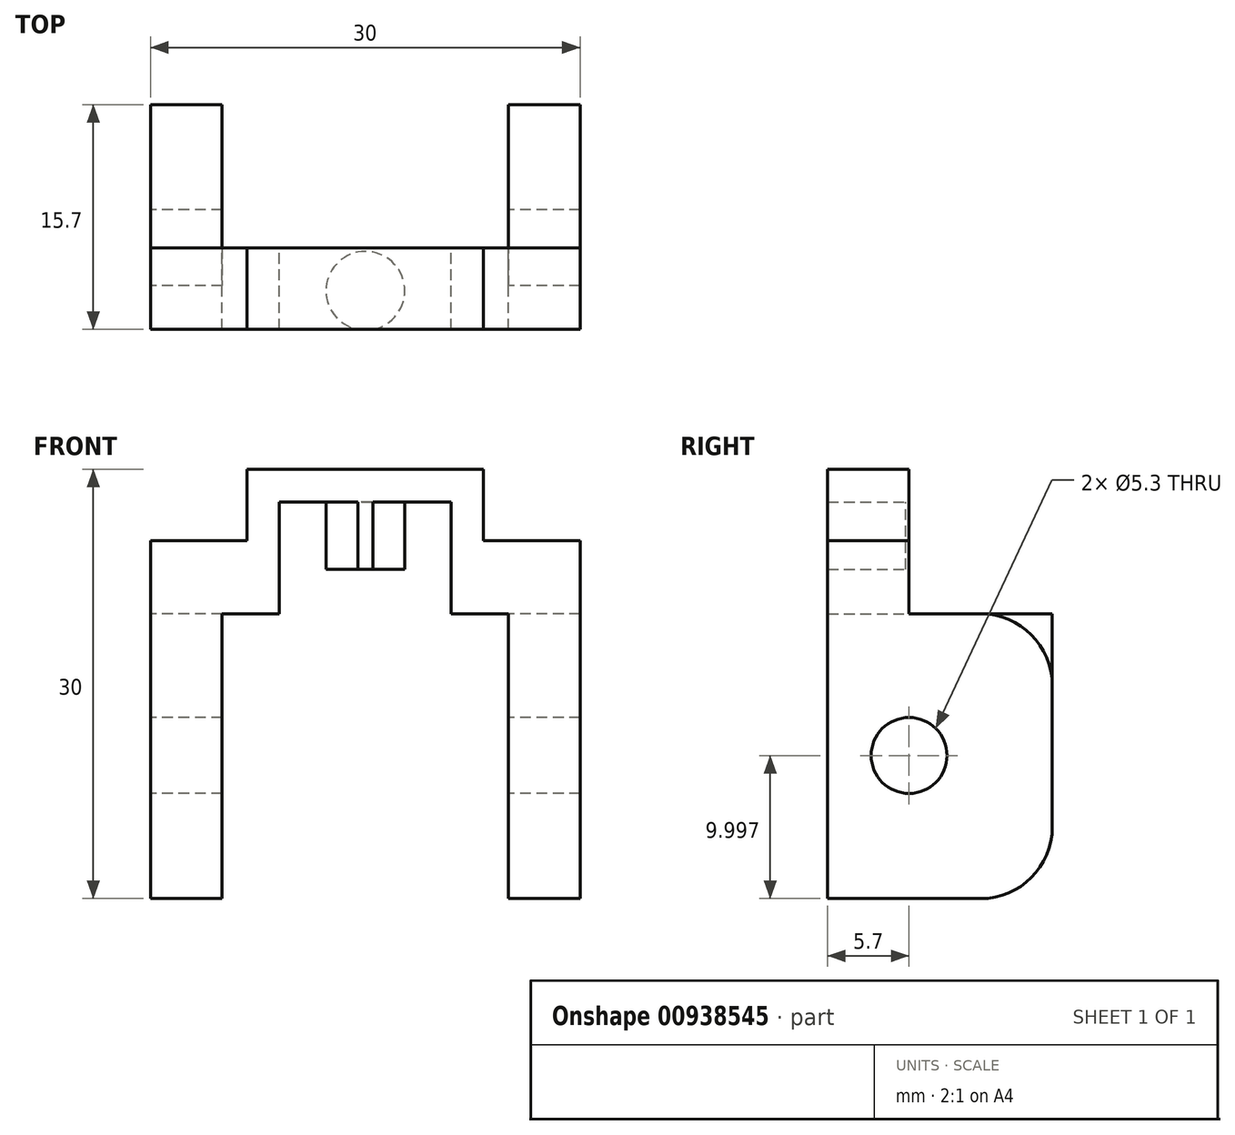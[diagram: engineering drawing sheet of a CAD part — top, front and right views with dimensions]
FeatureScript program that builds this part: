
annotation { "Feature Type Name" : "Feature", "Feature Type Description" : "" }
export const myFeature = defineFeature(function(context is Context, id is Id, definition is map)
    precondition{}
    {
        {
            var Q0;
            Q0=qCreatedBy(makeId("Front.planeOp"),FACE);
            var sketch = newSketch(context, id + "F0", { "sketchPlane" : qUnion([Q0])});
            skLineSegment(sketch, "E0.bottom", {"start": v(-7, 4.63) * mm, "end": v(-0.26, 4.63) * mm});
            skLineSegment(sketch, "E0.left", {"start": v(-7, 4.63) * mm, "end": v(-7, -20.37) * mm});
            skLineSegment(sketch, "E0.right", {"start": v(23, 4.63) * mm, "end": v(23, -20.37) * mm});
            skLineSegment(sketch, "E1.top", {"start": v(-0.26, 9.63) * mm, "end": v(16.24, 9.63) * mm});
            skLineSegment(sketch, "E1.left", {"start": v(-0.26, 4.63) * mm, "end": v(-0.26, 9.63) * mm});
            skLineSegment(sketch, "E1.right", {"start": v(16.24, 4.63) * mm, "end": v(16.24, 9.63) * mm});
            skPoint(sketch, "E2", {"position": v(8, 9.63) * mm});
            skPoint(sketch, "E3", {"position": v(8, -20.07) * mm});
            skLineSegment(sketch, "E4.trimOffspring", {"start": v(16.24, 4.63) * mm, "end": v(23, 4.63) * mm});
            skLineSegment(sketch, "E5.0", {"start": v(-2, -0.47) * mm, "end": v(-2, -20.37) * mm});
            skLineSegment(sketch, "E6.0", {"start": v(18, -0.47) * mm, "end": v(18, -20.37) * mm});
            skLineSegment(sketch, "E7.0", {"start": v(-2, -0.47) * mm, "end": v(2, -0.47) * mm});
            skLineSegment(sketch, "E8.0", {"start": v(14, -0.47) * mm, "end": v(18, -0.47) * mm});
            skLineSegment(sketch, "E9.0", {"start": v(2, -0.47) * mm, "end": v(2, 7.33) * mm});
            skLineSegment(sketch, "E10.0", {"start": v(14, -0.47) * mm, "end": v(14, 7.33) * mm});
            skLineSegment(sketch, "E11.0", {"start": v(2, 7.33) * mm, "end": v(14, 7.33) * mm});
            skLineSegment(sketch, "E12", {"start": v(-7, -20.37) * mm, "end": v(-2, -20.37) * mm});
            skLineSegment(sketch, "E13", {"start": v(23, -20.37) * mm, "end": v(18, -20.37) * mm});
            skSolve(sketch);
        }
        {
            var Q0;
            Q0 = qSketchRegion(id + "F0", true);
            extrude(context, id + "F1", {"entities" : qUnion([Q0]), "depth" : 20 * mm, "offsetDistance" : 25 * mm});
        }
        {
            var Q0;
            Q0=makeQuery(id+"F1.opExtrude","SWEPT_FACE",FACE,{"disambiguationData":[OSD([sQuery(id+"F0.wireOp",EDGE,"E0.left")])]});
            var sketch = newSketch(context, id + "F2", { "sketchPlane" : qUnion([Q0])});
            skCircle(sketch, "E14", {"center": v(10, -10.37) * mm, "radius": 2.65 * mm});
            skPoint(sketch, "E15", {"position": v(10, -20.37) * mm});
            skSolve(sketch);
        }
        {
            var Q0;
            Q0 = qSketchRegion(id + "F2", true);
            extrude(context, id + "F3", {"entities" : qUnion([Q0]), "operationType" : NewBodyOperationType.REMOVE, "endBound" : BoundingType.THROUGH_ALL, "oppositeDirection" : true, "depth" : 25 * mm, "offsetDistance" : 25 * mm});
        }
        {
            var Q0;
            Q0=makeQuery(id+"F1.opExtrude","SWEPT_FACE",FACE,{"disambiguationData":[OSD([sQuery(id+"F0.wireOp",EDGE,"E1.top")])]});
            var sketch = newSketch(context, id + "F4", { "sketchPlane" : qUnion([Q0])});
            skCircle(sketch, "E16", {"center": v(8, -13) * mm, "radius": 2.75 * mm});
            skLineSegment(sketch, "E17", {"start": v(-0.26, -20) * mm, "end": v(16.24, -20) * mm, "construction": true});
            skPoint(sketch, "E18", {"position": v(8, -20) * mm});
            skSolve(sketch);
        }
        {
            var Q0;
            Q0=makeQuery(id+"F4.imprint","IMPRINT",FACE,{"disambiguationData":[TD([[makeQuery(id+"F4.imprint","IMPRINT",EDGE,{"derivedFrom":sQuery(id+"F4.wireOp",EDGE,"E16")}),1.0]])]});
            extrude(context, id + "F5", {"entities" : qUnion([Q0]), "operationType" : NewBodyOperationType.ADD, "oppositeDirection" : true, "depth" : 7 * mm, "offsetDistance" : 25 * mm});
        }
        {
            var Q0;
            Q0=makeQuery(id+"F1.opExtrude","SWEPT_FACE",FACE,{"disambiguationData":[OSD([sQuery(id+"F0.wireOp",EDGE,"E1.top")])]});
            var sketch = newSketch(context, id + "F6", { "sketchPlane" : qUnion([Q0])});
            skLineSegment(sketch, "E19.0", {"start": v(-7, -20) * mm, "end": v(-7, 0) * mm, "construction": true});
            skLineSegment(sketch, "E20.0", {"start": v(23, -20) * mm, "end": v(23, 0) * mm, "construction": true});
            skLineSegment(sketch, "E21.bottom", {"start": v(-7, 0) * mm, "end": v(23, 0) * mm});
            skLineSegment(sketch, "E21.top", {"start": v(-7, -10) * mm, "end": v(23, -10) * mm});
            skLineSegment(sketch, "E21.left", {"start": v(-7, 0) * mm, "end": v(-7, -10) * mm});
            skLineSegment(sketch, "E21.right", {"start": v(23, 0) * mm, "end": v(23, -10) * mm});
            skSolve(sketch);
        }
        {
            var Q0;
            Q0 = qSketchRegion(id + "F6", true);
            var Q1;
            Q1=makeQuery(id+"F1.opExtrude","SWEPT_FACE",FACE,{"disambiguationData":[OSD([sQuery(id+"F0.wireOp",EDGE,"E8.0")])]});
            extrude(context, id + "F7", {"entities" : qUnion([Q0]), "operationType" : NewBodyOperationType.REMOVE, "endBound" : BoundingType.UP_TO_SURFACE, "oppositeDirection" : true, "depth" : 25 * mm, "endBoundEntityFace" : qUnion([Q1]), "offsetDistance" : 25 * mm});
        }
        {
            var Q0;
            Q0=makeQuery(id+"F1.opExtrude","SWEPT_FACE",FACE,{"disambiguationData":[OSD([sQuery(id+"F0.wireOp",EDGE,"E12")])]});
            var sketch = newSketch(context, id + "F8", { "sketchPlane" : qUnion([Q0])});
            skPoint(sketch, "E22.0", {"position": v(8, 20) * mm});
            skPoint(sketch, "E23.orphan", {"position": v(-7, 20) * mm});
            skLineSegment(sketch, "E24.0", {"start": v(23, 20) * mm, "end": v(23, 0) * mm, "construction": true});
            skLineSegment(sketch, "E25.0", {"start": v(-7, 20) * mm, "end": v(-7, 0) * mm, "construction": true});
            skLineSegment(sketch, "E26.bottom", {"start": v(-7, 20) * mm, "end": v(23, 20) * mm});
            skLineSegment(sketch, "E26.top", {"start": v(-7, 15.7) * mm, "end": v(23, 15.7) * mm});
            skLineSegment(sketch, "E26.left", {"start": v(-7, 20) * mm, "end": v(-7, 15.7) * mm});
            skLineSegment(sketch, "E26.right", {"start": v(23, 20) * mm, "end": v(23, 15.7) * mm});
            skSolve(sketch);
        }
        {
            var Q0;
            {var subQ1=sQuery(id+"F0.wireOp",EDGE,"E0.right");var subQ2=sQuery(id+"F6.wireOp",EDGE,"E21.bottom");Q0=makeQuery(id+"F7.boolean.opBoolean","COPY",EDGE,{"disambiguationData":[TD([makeQuery(id+"F1.opExtrude","SWEPT_FACE",FACE,{"disambiguationData":[OSD([subQ1])]})])],"derivedFrom":makeQuery(id+"F7.opExtrude","CAP_EDGE",EDGE,{"disambiguationData":[OSD([subQ2])],"isStart":false})});}
            var Q1;
            {var subQ1=sQuery(id+"F0.wireOp",EDGE,"E0.left");var subQ2=sQuery(id+"F6.wireOp",EDGE,"E21.bottom");Q1=makeQuery(id+"F7.boolean.opBoolean","COPY",EDGE,{"disambiguationData":[TD([makeQuery(id+"F1.opExtrude","SWEPT_FACE",FACE,{"disambiguationData":[OSD([subQ1])]})])],"derivedFrom":makeQuery(id+"F7.opExtrude","CAP_EDGE",EDGE,{"disambiguationData":[OSD([subQ2])],"isStart":false})});}
            fillet(context, id + "F9", {"entities" : qUnion([Q0, Q1]), "radius" : 5 * mm, "tangentPropagation" : true, "allowEdgeOverflow" : false});
        }
        {
            var Q0;
            Q0 = qSketchRegion(id + "F8", true);
            extrude(context, id + "F10", {"entities" : qUnion([Q0]), "operationType" : NewBodyOperationType.REMOVE, "endBound" : BoundingType.THROUGH_ALL, "oppositeDirection" : true, "depth" : 25 * mm, "offsetDistance" : 25 * mm});
        }
        {
            var Q0;
            Q0=makeQuery(id+"F1.opExtrude","CAP_EDGE",EDGE,{"disambiguationData":[OSD([sQuery(id+"F0.wireOp",EDGE,"E13")])],"isStart":true});
            var Q1;
            Q1=makeQuery(id+"F1.opExtrude","CAP_EDGE",EDGE,{"disambiguationData":[OSD([sQuery(id+"F0.wireOp",EDGE,"E12")])],"isStart":true});
            fillet(context, id + "F11", {"entities" : qUnion([Q0, Q1]), "radius" : 5 * mm, "tangentPropagation" : true, "allowEdgeOverflow" : false});
        }
    });
